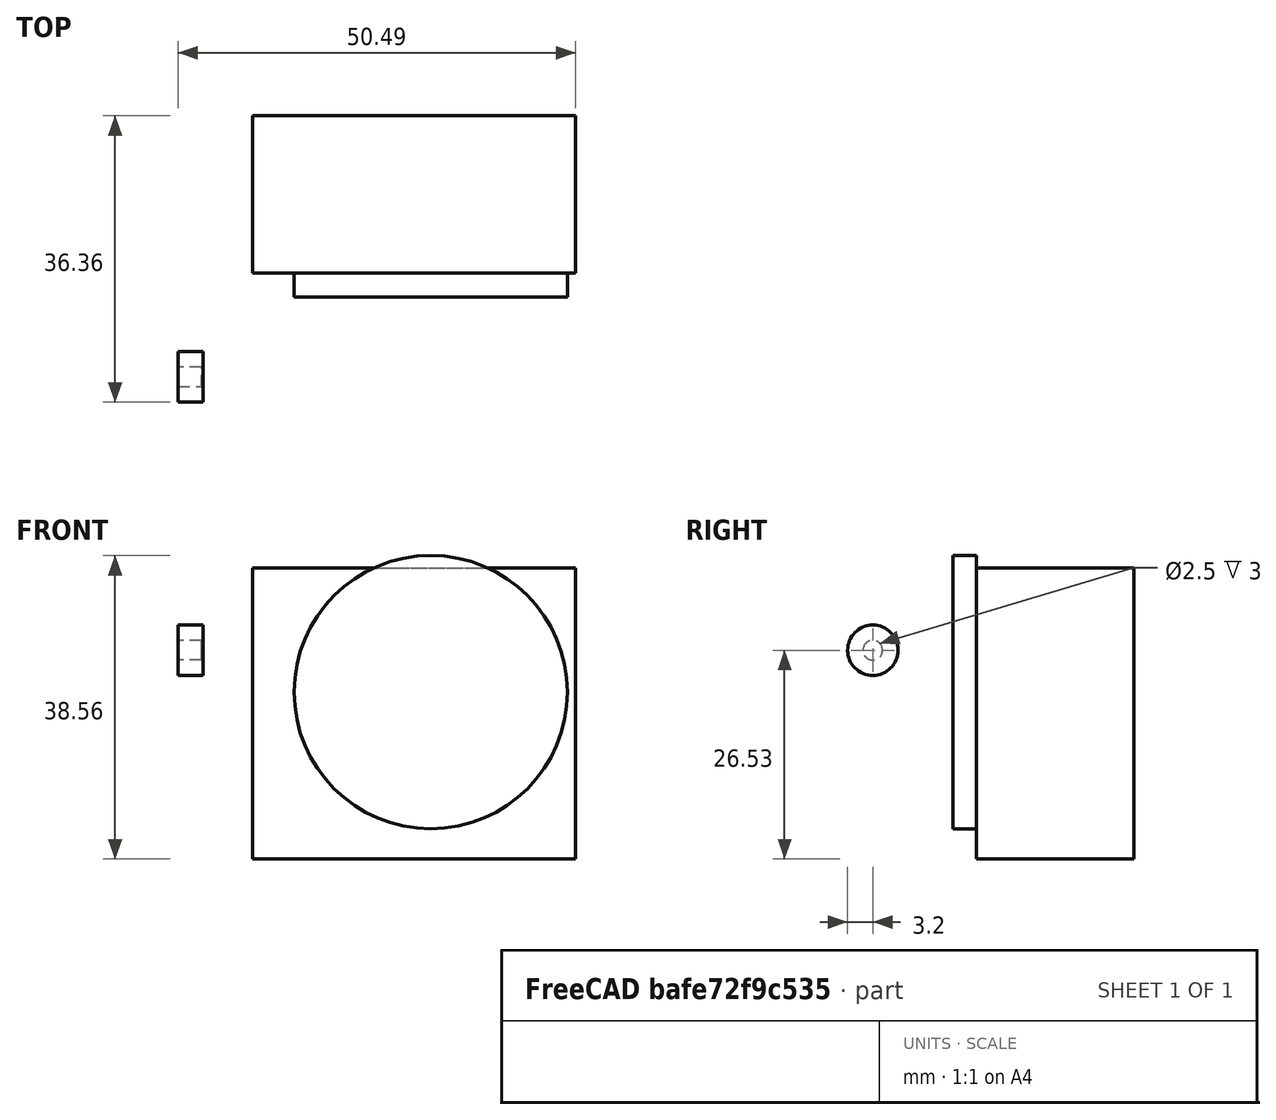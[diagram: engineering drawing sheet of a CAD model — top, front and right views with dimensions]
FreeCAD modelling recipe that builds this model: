
FCSTD DOCUMENT  (FreeCAD 0.18R4 (GitTag))
Label: Gimbal_ServoHolder
License: All rights reserved
LicenseURL: http://en.wikipedia.org/wiki/All_rights_reserved
objects: Sketcher::SketchObject×4, PartDesign::Pad×3, Part::Feature×2, PartDesign::Body×2, Mesh::Feature×1, PartDesign::ShapeBinder×1, PartDesign::Pocket×1
note: 17 computed .brp shape members not serialized (recipe doc carries the construction recipe); baked Part::Feature solids carry a one-line shape summary decoded from their .brp

FEATURE [Mesh::Feature] tilt
FEATURE [Part::Feature] tilt001
  shape: bbox 60.05 x 43.26 x 60.05 mm, 1862 faces, 0 solids (baked)
FEATURE [Part::Feature] tilt001001  label="tilt002"
  shape: bbox 60.05 x 43.26 x 60.05 mm, 469 faces, 0 solids (baked)
FEATURE [Sketcher::SketchObject] Sketch
  MapMode = 5
  Placement = pos=(0,0,0) rot=(1,0,0;1.5708rad)
  Support = -> [XZ_Plane]
  sketch-geometry (1):
    g0: Circle CenterX=32.1131 CenterY=34.7112 CenterZ=0 NormalX=0 NormalY=0 NormalZ=1 AngleXU=0 Radius=17.3521
FEATURE [PartDesign::Pad] Pad
  Length = 3
  Length2 = 100
  Placement = pos=(0,0,0) rot=(1,0,0;1.5708rad)
  Profile = -> Sketch
  Type = 0
FEATURE [Sketcher::SketchObject] Sketch001
  MapMode = 5
  Placement = pos=(0,1e-16,0) rot=(-1,0,0;1.5708rad)
  Support = -> [Pad]
  sketch-geometry (4):
    g0: LineSegment StartX=9.5 StartY=-50.5 StartZ=0 EndX=50.5 EndY=-50.5 EndZ=0
    g1: LineSegment StartX=50.5 StartY=-50.5 StartZ=0 EndX=50.5 EndY=-13.5 EndZ=0
    g2: LineSegment StartX=50.5 StartY=-13.5 StartZ=0 EndX=9.5 EndY=-13.5 EndZ=0
    g3: LineSegment StartX=9.5 StartY=-13.5 StartZ=0 EndX=9.5 EndY=-50.5 EndZ=0
  constraints (12):
    c: Coincident(g0,g1)
    c: Coincident(g1,g2)
    c: Coincident(g2,g3)
    c: Coincident(g3,g0)
    c: Horizontal(g0)
    c: Horizontal(g2)
    c: Vertical(g1)
    c: Vertical(g3)
    c: DistanceX(g2,g2) = 41
    c: DistanceX(g-1,g2) = 9.5
    c: DistanceY(g0,g-1) = 50.5
    c: DistanceY(g3,g3) = 37
FEATURE [PartDesign::Pad] Pad001
  BaseFeature = -> Pad
  Length = 20
  Length2 = 100
  Placement = pos=(0,0,0) rot=(1,0,0;1.5708rad)
  Profile = -> Sketch001
  Type = 0
FEATURE [PartDesign::Body] Body
  Group = -> [Sketch,Pad,Sketch001,Pad001]
  Origin = -> Origin
  Placement = pos=(0,23.16,0) rot=(0,0,1;0rad)
  Tip = -> Pad001
FEATURE [PartDesign::ShapeBinder] Copytilt001001
  TraceSupport = false
FEATURE [Sketcher::SketchObject] Sketch002
  MapMode = 5
  Placement = pos=(3.17503,0,0) rot=(0.57735,-0.57735,-0.57735;2.0944rad)
  Support = -> [Copytilt001001]
  sketch-geometry (1):
    g0: Circle CenterX=-10 CenterY=40.03 CenterZ=0 NormalX=0 NormalY=0 NormalZ=1 AngleXU=0 Radius=3.2
  constraints (3):
    c: DistanceX(g0,g-1) = 10
    c: DistanceY(g-1,g0) = 40.03
    c: Radius(g0) = 3.2
FEATURE [PartDesign::Pad] Pad002
  Length = 3.17
  Length2 = 100
  Profile = -> Sketch002
  Type = 0
FEATURE [Sketcher::SketchObject] Sketch003
  MapMode = 5
  Placement = pos=(0.00502761,0,0) rot=(0.57735,-0.57735,-0.57735;2.0944rad)
  Support = -> [Pad002]
  sketch-geometry (1):
    g0: Circle CenterX=-10 CenterY=40.03 CenterZ=0 NormalX=0 NormalY=0 NormalZ=1 AngleXU=0 Radius=1.25
  constraints (3):
    c: Radius(g0) = 1.25
    c: DistanceY(g-1,g0) = 40.03
    c: DistanceX(g0,g-1) = 10
FEATURE [PartDesign::Pocket] Pocket
  BaseFeature = -> Pad002
  Length = 3
  Length2 = 100
  Profile = -> Sketch003
  Type = 0
FEATURE [PartDesign::Body] Body001
  Group = -> [Copytilt001001,Sketch002,Pad002,Sketch003,Pocket]
  Origin = -> Origin001
  Tip = -> Pocket
